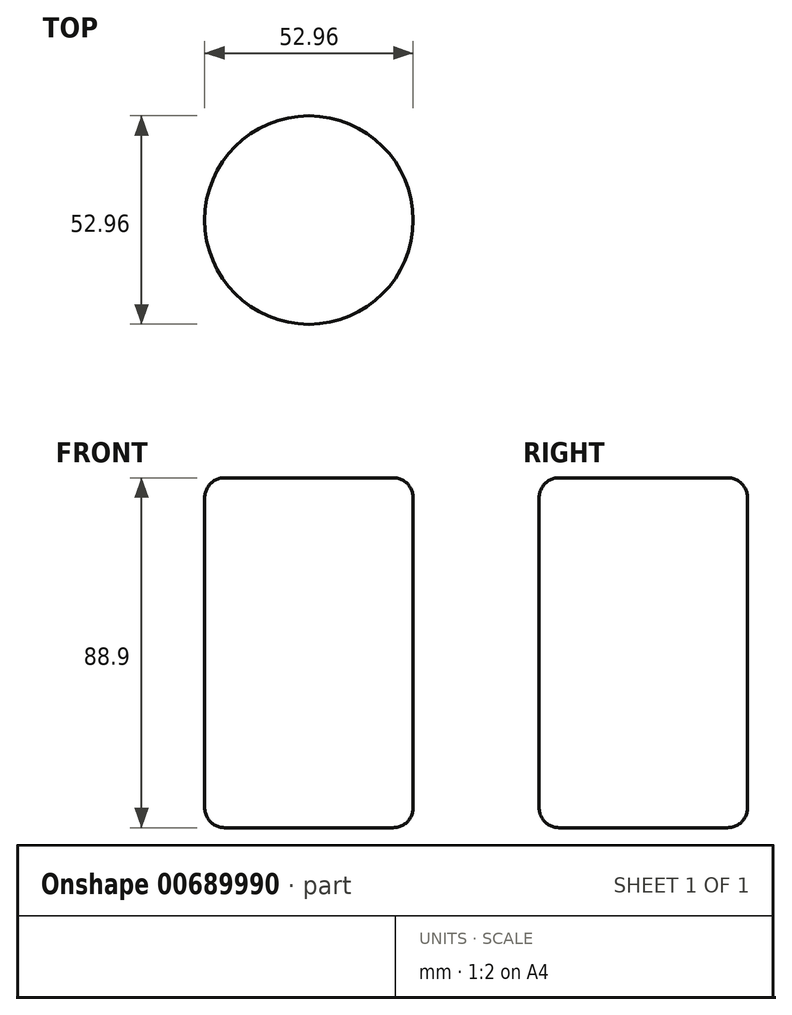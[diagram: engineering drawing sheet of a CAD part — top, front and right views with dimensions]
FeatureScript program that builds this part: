
annotation { "Feature Type Name" : "Feature", "Feature Type Description" : "" }
export const myFeature = defineFeature(function(context is Context, id is Id, definition is map)
    precondition{}
    {
        {
            var Q0;
            Q0=qCreatedBy(makeId("Top.planeOp"),FACE);
            var sketch = newSketch(context, id + "F0", { "sketchPlane" : qUnion([Q0])});
            skCircle(sketch, "E0", {"center": v(0, 0) * mm, "radius": 26.48 * mm});
            skSolve(sketch);
        }
        {
            var Q0;
            Q0=makeQuery(id+"F0.imprint","IMPRINT",FACE,{"disambiguationData":[TD([[makeQuery(id+"F0.imprint","IMPRINT",EDGE,{"derivedFrom":sQuery(id+"F0.wireOp",EDGE,"E0")}),1.0]])]});
            extrude(context, id + "F1", {"entities" : qUnion([Q0]), "depth" : 88.9 * mm, "offsetDistance" : 25.4 * mm});
        }
        {
            var Q0;
            Q0=makeQuery(id+"F1.opExtrude","CAP_EDGE",EDGE,{"disambiguationData":[OSD([sQuery(id+"F0.wireOp",EDGE,"E0")])],"isStart":false});
            var Q1;
            Q1=makeQuery(id+"F1.opExtrude","SWEPT_FACE",FACE,{"disambiguationData":[OSD([sQuery(id+"F0.wireOp",EDGE,"E0")])]});
            fillet(context, id + "F2", {"entities" : qUnion([Q0, Q1]), "radius" : 5.08 * mm, "tangentPropagation" : true, "allowEdgeOverflow" : false});
        }
    });
